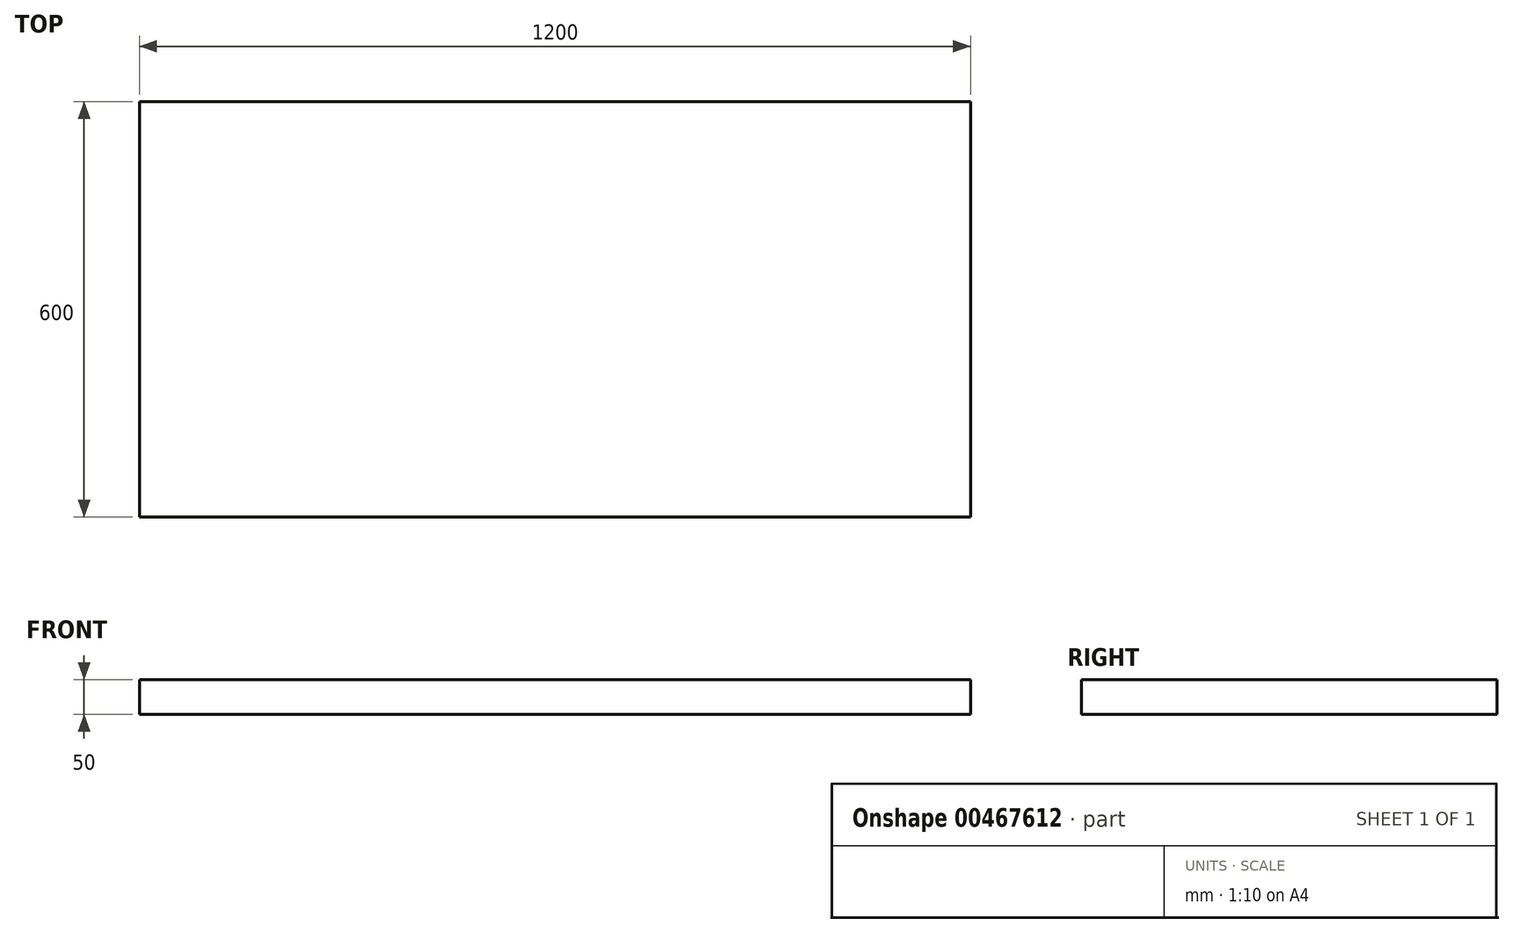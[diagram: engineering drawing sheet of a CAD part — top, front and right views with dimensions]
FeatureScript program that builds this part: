
annotation { "Feature Type Name" : "Feature", "Feature Type Description" : "" }
export const myFeature = defineFeature(function(context is Context, id is Id, definition is map)
    precondition{}
    {
        {
            var Q0;
            Q0=qCreatedBy(makeId("Top.planeOp"),FACE);
            var sketch = newSketch(context, id + "F0", { "sketchPlane" : qUnion([Q0])});
            skLineSegment(sketch, "E0.bottom", {"start": v(-730.94, 0) * mm, "end": v(469.06, 0) * mm});
            skLineSegment(sketch, "E0.top", {"start": v(-730.94, -600) * mm, "end": v(469.06, -600) * mm});
            skLineSegment(sketch, "E0.left", {"start": v(-730.94, 0) * mm, "end": v(-730.94, -600) * mm});
            skLineSegment(sketch, "E0.right", {"start": v(469.06, 0) * mm, "end": v(469.06, -600) * mm});
            skSolve(sketch);
        }
        {
            var Q0;
            Q0 = qSketchRegion(id + "F0", true);
            extrude(context, id + "F1", {"entities" : qUnion([Q0]), "depth" : 50 * mm});
        }
    });
